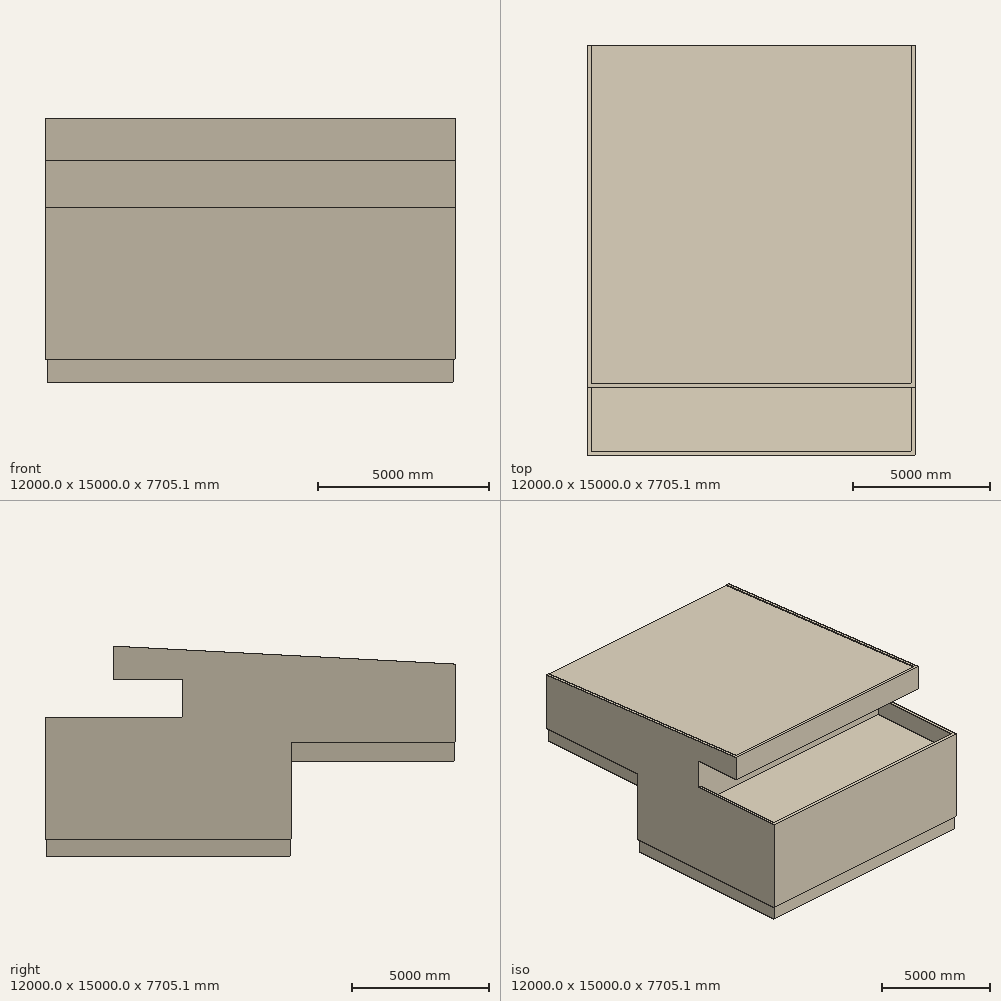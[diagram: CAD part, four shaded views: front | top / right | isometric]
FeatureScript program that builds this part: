
annotation { "Feature Type Name" : "Feature", "Feature Type Description" : "" }
export const myFeature = defineFeature(function(context is Context, id is Id, definition is map)
    precondition{}
    {
        {
            var Q0;
            Q0=qCreatedBy(makeId("Top.planeOp"),FACE);
            var sketch = newSketch(context, id + "F0", { "sketchPlane" : qUnion([Q0])});
            skLineSegment(sketch, "E0.bottom", {"start": v(5950, 4450) * mm, "end": v(-5950, 4450) * mm});
            skLineSegment(sketch, "E0.top", {"start": v(5950, -4450) * mm, "end": v(-5950, -4450) * mm});
            skLineSegment(sketch, "E0.left", {"start": v(5950, 4450) * mm, "end": v(5950, -4450) * mm});
            skLineSegment(sketch, "E0.right", {"start": v(-5950, 4450) * mm, "end": v(-5950, -4450) * mm});
            skPoint(sketch, "E0.middle", {"position": v(0, 0) * mm});
            skSolve(sketch);
        }
        {
            var Q0;
            Q0 = qSketchRegion(id + "F0", true);
            extrude(context, id + "F1", {"entities" : qUnion([Q0]), "depth" : 650 * mm, "offsetDistance" : 25 * mm});
        }
        {
            var Q0;
            Q0=makeQuery(id+"F1.opExtrude","CAP_FACE",FACE,{"disambiguationData":[OSD([sQuery(id+"F0.wireOp",EDGE,"E0.bottom"),sQuery(id+"F0.wireOp",EDGE,"E0.top"),sQuery(id+"F0.wireOp",EDGE,"E0.left"),sQuery(id+"F0.wireOp",EDGE,"E0.right")])],"isStart":false});
            var sketch = newSketch(context, id + "F2", { "sketchPlane" : qUnion([Q0])});
            skLineSegment(sketch, "E1.bottom", {"start": v(6000, 4500) * mm, "end": v(-6000, 4500) * mm});
            skLineSegment(sketch, "E1.top", {"start": v(6000, -4500) * mm, "end": v(-6000, -4500) * mm});
            skLineSegment(sketch, "E1.left", {"start": v(6000, 4500) * mm, "end": v(6000, -4500) * mm});
            skLineSegment(sketch, "E1.right", {"start": v(-6000, 4500) * mm, "end": v(-6000, -4500) * mm});
            skPoint(sketch, "E1.middle", {"position": v(0, 0) * mm});
            skSolve(sketch);
        }
        {
            var Q0;
            Q0 = qSketchRegion(id + "F2", true);
            extrude(context, id + "F3", {"entities" : qUnion([Q0]), "operationType" : NewBodyOperationType.ADD, "depth" : 3500 * mm, "offsetDistance" : 25 * mm});
        }
        {
            var Q0;
            Q0 = qSketchRegion(id + "F2", true);
            extrude(context, id + "F4", {"entities" : qUnion([Q0]), "operationType" : NewBodyOperationType.ADD, "depth" : 3500 * mm, "offsetDistance" : 25 * mm});
        }
        {
            var Q0;
            Q0=makeQuery(id+"F3.opExtrude","CAP_FACE",FACE,{"disambiguationData":[OSD([sQuery(id+"F2.wireOp",EDGE,"E1.bottom"),sQuery(id+"F2.wireOp",EDGE,"E1.top"),sQuery(id+"F2.wireOp",EDGE,"E1.left"),sQuery(id+"F2.wireOp",EDGE,"E1.right")])],"isStart":false});
            var sketch = newSketch(context, id + "F5", { "sketchPlane" : qUnion([Q0])});
            skLineSegment(sketch, "E2.bottom", {"start": v(-5950, 4500) * mm, "end": v(5950, 4500) * mm});
            skLineSegment(sketch, "E2.top", {"start": v(-5950, 10450) * mm, "end": v(5950, 10450) * mm});
            skLineSegment(sketch, "E2.left", {"start": v(-5950, 4500) * mm, "end": v(-5950, 10450) * mm});
            skLineSegment(sketch, "E2.right", {"start": v(5950, 4500) * mm, "end": v(5950, 10450) * mm});
            skSolve(sketch);
        }
        {
            var Q0;
            Q0 = qSketchRegion(id + "F5", true);
            extrude(context, id + "F6", {"entities" : qUnion([Q0]), "operationType" : NewBodyOperationType.ADD, "oppositeDirection" : true, "depth" : 650 * mm, "offsetDistance" : 25 * mm});
        }
        {
            var Q0;
            Q0=makeQuery(id+"F6.boolean.opBoolean","MERGE",FACE,{"derivedFrom":[makeQuery(id+"F3.opExtrude","CAP_FACE",FACE,{"disambiguationData":[OSD([sQuery(id+"F2.wireOp",EDGE,"E1.bottom"),sQuery(id+"F2.wireOp",EDGE,"E1.top"),sQuery(id+"F2.wireOp",EDGE,"E1.left"),sQuery(id+"F2.wireOp",EDGE,"E1.right")])],"isStart":false}),makeQuery(id+"F6.opExtrude","CAP_FACE",FACE,{"disambiguationData":[OSD([sQuery(id+"F5.wireOp",EDGE,"E2.bottom"),sQuery(id+"F5.wireOp",EDGE,"E2.top"),sQuery(id+"F5.wireOp",EDGE,"E2.left"),sQuery(id+"F5.wireOp",EDGE,"E2.right")])],"isStart":true})]});
            extrude(context, id + "F7", {"entities" : qUnion([Q0]), "operationType" : NewBodyOperationType.ADD, "depth" : 25 * mm, "offsetDistance" : 25 * mm});
        }
        {
            var Q0;
            Q0=makeQuery(id+"F7.opExtrude","CAP_FACE",FACE,{"disambiguationData":[OSD([sQuery(id+"F2.wireOp",EDGE,"E1.bottom"),sQuery(id+"F2.wireOp",EDGE,"E1.top"),sQuery(id+"F2.wireOp",EDGE,"E1.left"),sQuery(id+"F2.wireOp",EDGE,"E1.right"),sQuery(id+"F5.wireOp",EDGE,"E2.bottom"),sQuery(id+"F5.wireOp",EDGE,"E2.top"),sQuery(id+"F5.wireOp",EDGE,"E2.left"),sQuery(id+"F5.wireOp",EDGE,"E2.right")])],"isStart":false});
            var sketch = newSketch(context, id + "F8", { "sketchPlane" : qUnion([Q0])});
            skLineSegment(sketch, "E3.bottom", {"start": v(-6000, -4500) * mm, "end": v(6000, -4500) * mm});
            skLineSegment(sketch, "E3.top", {"start": v(-6000, 10500) * mm, "end": v(6000, 10500) * mm});
            skLineSegment(sketch, "E3.left", {"start": v(-6000, -4500) * mm, "end": v(-6000, 10500) * mm});
            skLineSegment(sketch, "E3.right", {"start": v(6000, -4500) * mm, "end": v(6000, 10500) * mm});
            skLineSegment(sketch, "E4.bottom", {"start": v(-5850, -4350) * mm, "end": v(5850, -4350) * mm});
            skLineSegment(sketch, "E4.top", {"start": v(-5850, 500) * mm, "end": v(5850, 500) * mm});
            skLineSegment(sketch, "E4.left", {"start": v(-5850, -4350) * mm, "end": v(-5850, 500) * mm});
            skLineSegment(sketch, "E4.right", {"start": v(5850, -4350) * mm, "end": v(5850, 500) * mm});
            skSolve(sketch);
        }
        {
            var Q0;
            Q0 = qSketchRegion(id + "F8", true);
            extrude(context, id + "F9", {"entities" : qUnion([Q0]), "operationType" : NewBodyOperationType.ADD, "depth" : 2300 * mm, "offsetDistance" : 25 * mm});
        }
        {
            var Q0;
            Q0=makeQuery(id+"F9.opExtrude","CAP_FACE",FACE,{"disambiguationData":[OSD([sQuery(id+"F8.wireOp",EDGE,"E3.bottom"),sQuery(id+"F8.wireOp",EDGE,"E3.top"),sQuery(id+"F8.wireOp",EDGE,"E3.left"),sQuery(id+"F8.wireOp",EDGE,"E3.right"),sQuery(id+"F8.wireOp",EDGE,"E4.bottom"),sQuery(id+"F8.wireOp",EDGE,"E4.top"),sQuery(id+"F8.wireOp",EDGE,"E4.left"),sQuery(id+"F8.wireOp",EDGE,"E4.right")])],"isStart":false});
            extrude(context, id + "F10", {"entities" : qUnion([Q0]), "operationType" : NewBodyOperationType.ADD, "depth" : 25 * mm, "offsetDistance" : 25 * mm});
        }
        {
            var Q0;
            Q0=makeQuery(id+"F10.opExtrude","CAP_FACE",FACE,{"disambiguationData":[OSD([sQuery(id+"F8.wireOp",EDGE,"E3.bottom"),sQuery(id+"F8.wireOp",EDGE,"E3.top"),sQuery(id+"F8.wireOp",EDGE,"E3.left"),sQuery(id+"F8.wireOp",EDGE,"E3.right"),sQuery(id+"F8.wireOp",EDGE,"E4.bottom"),sQuery(id+"F8.wireOp",EDGE,"E4.top"),sQuery(id+"F8.wireOp",EDGE,"E4.left"),sQuery(id+"F8.wireOp",EDGE,"E4.right")])],"isStart":false});
            var sketch = newSketch(context, id + "F11", { "sketchPlane" : qUnion([Q0])});
            skLineSegment(sketch, "E5.bottom", {"start": v(-6000, -4500) * mm, "end": v(6000, -4500) * mm});
            skLineSegment(sketch, "E5.top", {"start": v(-6000, 500) * mm, "end": v(6000, 500) * mm});
            skLineSegment(sketch, "E5.left", {"start": v(-6000, -4500) * mm, "end": v(-6000, 500) * mm});
            skLineSegment(sketch, "E5.right", {"start": v(6000, -4500) * mm, "end": v(6000, 500) * mm});
            skSolve(sketch);
        }
        {
            var Q0;
            Q0 = qSketchRegion(id + "F11", true);
            extrude(context, id + "F12", {"entities" : qUnion([Q0]), "operationType" : NewBodyOperationType.REMOVE, "oppositeDirection" : true, "depth" : 1400 * mm, "offsetDistance" : 25 * mm});
        }
        {
            var Q0;
            {var subQ0=sQuery(id+"F8.wireOp",EDGE,"E3.right");var subQ1=sQuery(id+"F2.wireOp",EDGE,"E1.left");Q0=makeQuery(id+"F10.boolean.opBoolean","MERGE",FACE,{"derivedFrom":[makeQuery(id+"F9.boolean.opBoolean","MERGE",FACE,{"derivedFrom":[makeQuery(id+"F7.boolean.opBoolean","MERGE",FACE,{"derivedFrom":[makeQuery(id+"F3.opExtrude","SWEPT_FACE",FACE,{"disambiguationData":[OSD([subQ1])]}),makeQuery(id+"F7.opExtrude","SWEPT_FACE",FACE,{"disambiguationData":[OSD([subQ1])]})]}),makeQuery(id+"F9.opExtrude","SWEPT_FACE",FACE,{"disambiguationData":[OSD([subQ0])]})]}),makeQuery(id+"F10.opExtrude","SWEPT_FACE",FACE,{"disambiguationData":[OSD([subQ0])]})]});}
            var sketch = newSketch(context, id + "F13", { "sketchPlane" : qUnion([Q0])});
            skLineSegment(sketch, "E6", {"start": v(10500, 6500) * mm, "end": v(10500, 7050) * mm});
            skLineSegment(sketch, "E7", {"start": v(10500, 7050) * mm, "end": v(-2000, 7705.1) * mm});
            skLineSegment(sketch, "E8", {"start": v(-2000, 7705.1) * mm, "end": v(-2000, 6500) * mm});
            skLineSegment(sketch, "E9", {"start": v(-2000, 6500) * mm, "end": v(500, 6500) * mm});
            skLineSegment(sketch, "E10", {"start": v(500, 6500) * mm, "end": v(10500, 6500) * mm});
            skSolve(sketch);
        }
        {
            var Q0;
            Q0 = qSketchRegion(id + "F13", true);
            var Q1;
            {var subQ0=sQuery(id+"F8.wireOp",EDGE,"E3.left");var subQ1=sQuery(id+"F2.wireOp",EDGE,"E1.right");Q1=makeQuery(id+"F10.boolean.opBoolean","MERGE",FACE,{"derivedFrom":[makeQuery(id+"F9.boolean.opBoolean","MERGE",FACE,{"derivedFrom":[makeQuery(id+"F7.boolean.opBoolean","MERGE",FACE,{"derivedFrom":[makeQuery(id+"F3.opExtrude","SWEPT_FACE",FACE,{"disambiguationData":[OSD([subQ1])]}),makeQuery(id+"F7.opExtrude","SWEPT_FACE",FACE,{"disambiguationData":[OSD([subQ1])]})]}),makeQuery(id+"F9.opExtrude","SWEPT_FACE",FACE,{"disambiguationData":[OSD([subQ0])]})]}),makeQuery(id+"F10.opExtrude","SWEPT_FACE",FACE,{"disambiguationData":[OSD([subQ0])]})]});}
            extrude(context, id + "F14", {"entities" : qUnion([Q0]), "operationType" : NewBodyOperationType.ADD, "endBound" : BoundingType.UP_TO_SURFACE, "oppositeDirection" : true, "depth" : 25 * mm, "endBoundEntityFace" : qUnion([Q1]), "offsetDistance" : 25 * mm});
        }
        {
            var Q0;
            Q0=qCreatedBy(makeId("Right.planeOp"),FACE);
            var sketch = newSketch(context, id + "F15", { "sketchPlane" : qUnion([Q0])});
            skLineSegment(sketch, "E11", {"start": v(10500, 7075.03) * mm, "end": v(10500, 7024.97) * mm});
            skLineSegment(sketch, "E12", {"start": v(10500, 7024.97) * mm, "end": v(-1850, 7672.2) * mm});
            skLineSegment(sketch, "E13", {"start": v(-1850, 7672.2) * mm, "end": v(-1850, 7722.27) * mm});
            skLineSegment(sketch, "E14", {"start": v(-1850, 7722.27) * mm, "end": v(10500, 7075.03) * mm});
            skSolve(sketch);
        }
        {
            var Q0;
            Q0 = qSketchRegion(id + "F15", true);
            extrude(context, id + "F16", {"entities" : qUnion([Q0]), "operationType" : NewBodyOperationType.REMOVE, "endBound" : BoundingType.SYMMETRIC, "oppositeDirection" : true, "depth" : 11700 * mm, "offsetDistance" : 25 * mm});
        }
    });
